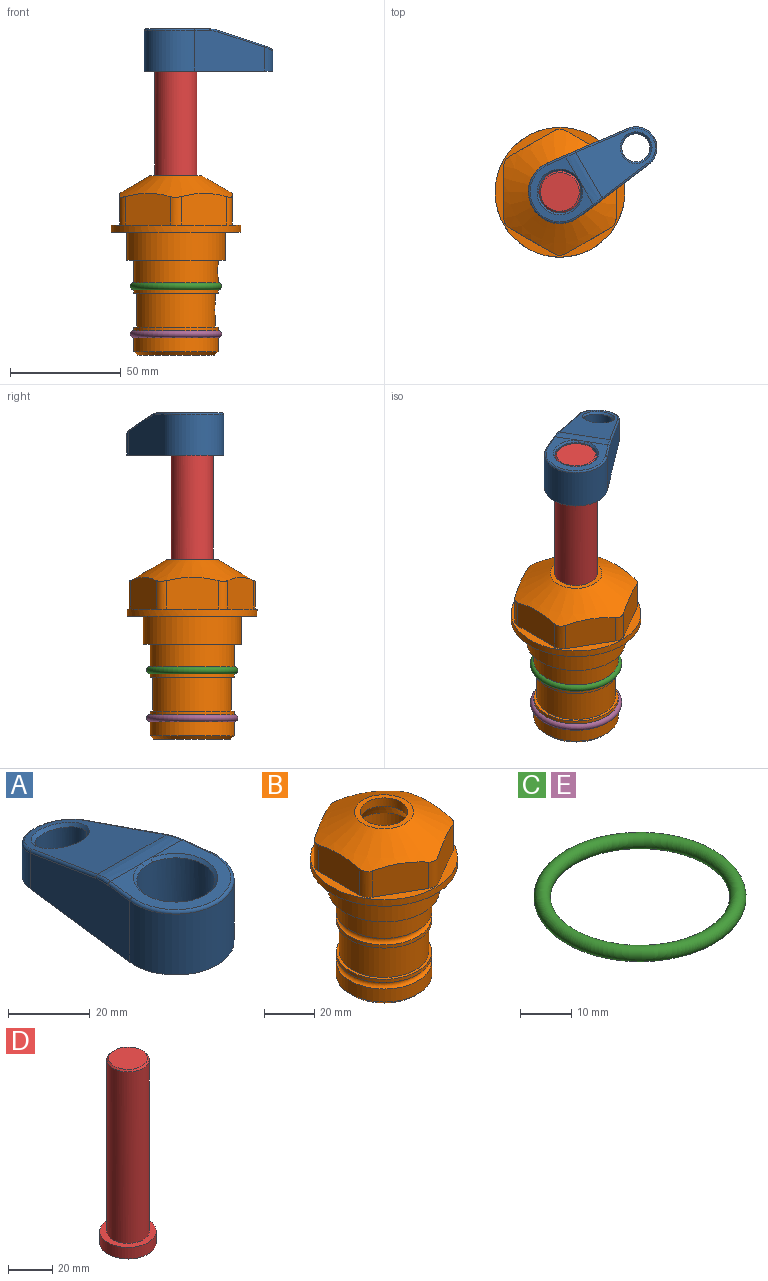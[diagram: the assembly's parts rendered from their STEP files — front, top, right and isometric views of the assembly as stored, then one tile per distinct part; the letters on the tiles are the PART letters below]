
ASSEMBLY  parts=5 mates=4
PART A: 31 faces, bbox 31.7x65.5x19.8 mm
  f0: plane 39.12x18.26mm, normal (0.99,0.12,0), area 612.2mm2, adj f1,f4,f7,f11,f13,f15
  f1: cylinder r=9.53mm len=18.91mm, axis (0,0,-1), area 296.1mm2, adj f0,f2,f7,f17
  f2: plane 39.12x18.26mm, normal (-0.99,0.12,0), area 612.2mm2, adj f1,f4,f7,f12,f14,f16
  f3: cylinder r=6.35mm len=12.7mm, axis (0,0,-1), area 362.4mm2, adj f7,f18
  f4: cylinder r=14.29mm len=28.58mm, axis (0,0,-1), area 882.2mm2, adj f0,f2,f7,f10
  f5: cylinder r=9.53mm len=19.05mm, axis (0,0,-1), area 1092.6mm2, adj f7,f19,f20
  f6: plane 26.99x23.69mm, normal (0,0,1), area 216.2mm2, adj f9,f10,f11,f12,f19
  f7: plane 63.5x28.58mm, normal (0,0,-1), area 661.8mm2, adj f0,f1,f2,f3,f4,f5,f22,f23
  f8: plane 33.52x23.6mm, normal (0,0.26,0.97), area 486mm2, adj f9,f15,f16,f17,f18
  f9: cylinder r=19.05mm len=24.72mm, axis (1,0,0), area 120.4mm2, adj f6,f8,f13,f14,f20
  f10: torus R=13.49mm, axis (0,0,1), area 59mm2, adj f4,f6,f11,f12
  f11: cylinder r=0.79mm len=8.67mm, axis (0.12,-0.99,0), area 10.8mm2, adj f0,f6,f10,f13
  f12: cylinder r=0.79mm len=8.67mm, axis (0.12,0.99,0), area 10.8mm2, adj f2,f6,f10,f14
  f13: bspline ~4.95x1.42mm, area 6.1mm2, adj f0,f9,f11,f15
  f14: bspline ~4.95x1.42mm, area 6.1mm2, adj f2,f9,f12,f16
  f15: cylinder r=0.79mm len=25.95mm, axis (0.12,-0.96,0.26), area 32.9mm2, adj f0,f8,f13,f17
  f16: cylinder r=0.79mm len=25.95mm, axis (0.12,0.96,-0.26), area 32.9mm2, adj f2,f8,f14,f17
  f17: bspline ~18.91x8.38mm, area 30mm2, adj f1,f8,f15,f16
  f18: bspline ~14.29x14.29mm, area 48.3mm2, adj f3,f8
  f19: cone r=9.53mm half-angle=45deg, axis (0,0,1), area 66.5mm2, adj f5,f6,f20
  f20: bspline ~3.22x0.96mm, area 3.5mm2, adj f5,f9,f19
  f21: plane 2.75x2.72mm, normal (0,0,-1), area 2.9mm2, adj f23,f25,f28
  f22: plane 23.05x15.88mm, normal (-0.99,-0.12,0), area 323.6mm2, adj f7,f25,f26,f27,f28,f29
  f23: plane 23.05x15.88mm, normal (0.99,-0.12,0), area 323.6mm2, adj f7,f21,f25,f27,f28,f30
  f24: cylinder r=9.53mm len=10.69mm, axis (0,0,-1), area 114.7mm2, adj f7,f27,f29,f30
  f25: cylinder r=12.7mm len=20.59mm, axis (0,0,-1), area 381.1mm2, adj f7,f21,f22,f23,f26,f28
  f26: plane 2.75x2.72mm, normal (0,0,-1), area 2.9mm2, adj f22,f25,f28
  f27: plane 19.72x18.37mm, normal (0,-0.26,-0.97), area 291.8mm2, adj f22,f23,f24,f28,f29,f30
  f28: cylinder r=15.88mm len=19.92mm, axis (1,0,0), area 54.8mm2, adj f21,f22,f23,f25,f26,f27
  f29: cylinder r=1.59mm len=11mm, axis (0,0,-1), area 34.7mm2, adj f7,f22,f24,f27
  f30: cylinder r=1.59mm len=11mm, axis (0,0,-1), area 34.7mm2, adj f7,f23,f24,f27
PART B: 36 faces, bbox 58.7x58.7x81 mm
  f0: cylinder r=17.78mm len=35.56mm, axis (0,0,1), area 1670.8mm2, adj f23,f24,f31
  f1: cylinder r=19.05mm len=38.1mm, axis (0,0,1), area 1191.9mm2, adj f26,f27,f30
  f2: plane 58.66x58.66mm, normal (0,0,-1), area 1150.6mm2, adj f3,f28
  f3: cylinder r=29.33mm len=58.66mm, axis (0,0,-1), area 585.1mm2, adj f2,f4
  f4: plane 58.66x58.66mm, normal (0,0,1), area 475.9mm2, adj f3,f5,f6,f7,f8,f9,f10,f11
  f5: plane 20.32x14.34mm, normal (-0.5,0.87,0), area 324.4mm2, adj f4,f15,f16,f17
  f6: plane 20.32x14.34mm, normal (0.5,0.87,0), area 324.4mm2, adj f4,f14,f15,f17
  f7: plane 23.48x14.34mm, normal (1,0,0), area 324.4mm2, adj f4,f13,f14,f17
  f8: plane 20.32x14.34mm, normal (0.5,-0.87,0), area 324.4mm2, adj f4,f12,f13,f17
  f9: plane 20.32x14.34mm, normal (-0.5,-0.87,0), area 324.4mm2, adj f4,f11,f12,f17
  f10: plane 23.48x14.34mm, normal (-1,0,0), area 324.4mm2, adj f4,f11,f16,f17
  f11: cylinder r=5.08mm len=12.85mm, axis (0,0,-1), area 67.2mm2, adj f4,f9,f10,f17
  f12: cylinder r=5.08mm len=12.85mm, axis (0,0,-1), area 67.2mm2, adj f4,f8,f9,f17
  f13: cylinder r=5.08mm len=12.85mm, axis (0,0,-1), area 67.2mm2, adj f4,f7,f8,f17
  f14: cylinder r=5.08mm len=12.85mm, axis (0,0,-1), area 67.2mm2, adj f4,f6,f7,f17
  f15: cylinder r=5.08mm len=12.85mm, axis (0,0,-1), area 67.2mm2, adj f4,f5,f6,f17
  f16: cylinder r=5.08mm len=12.85mm, axis (0,0,-1), area 67.2mm2, adj f4,f5,f10,f17
  f17: cone r=11.73mm half-angle=60deg, axis (0,0,-1), area 2071.8mm2, adj f5,f6,f7,f8,f9,f10,f11,f12
  f18: plane 23.46x23.46mm, normal (0,0,1), area 147.4mm2, adj f17,f35
  f19: plane 34.93x34.93mm, normal (0,0,-1), area 958mm2, adj f29
  f20: cylinder r=19.05mm len=38.1mm, axis (0,0,1), area 760.1mm2, adj f21,f29
  f21: torus R=19.05mm, axis (0,0,1), area 565.3mm2, adj f20,f22
  f22: cylinder r=19.05mm len=38.1mm, axis (0,0,1), area 190mm2, adj f21,f23
  f23: plane 38.1x38.1mm, normal (0,0,1), area 146.9mm2, adj f0,f22
  f24: plane 38.1x38.1mm, normal (0,0,-1), area 146.9mm2, adj f0,f25
  f25: cylinder r=19.05mm len=38.1mm, axis (0,0,1), area 190mm2, adj f24,f26
  f26: torus R=19.05mm, axis (0,0,1), area 565.3mm2, adj f1,f25
  f27: plane 44.45x44.45mm, normal (0,0,-1), area 411.7mm2, adj f1,f28
  f28: cylinder r=22.23mm len=44.45mm, axis (0,0,1), area 1773.5mm2, adj f2,f27
  f29: cone r=19.05mm half-angle=45deg, axis (0,0,1), area 257.5mm2, adj f19,f20
  f30: cylinder r=3.17mm len=6.75mm, axis (-1,0,0), area 128mm2, adj f1,f33
  f31: cylinder r=3.17mm len=6.35mm, axis (-1,0,0), area 102.5mm2, adj f0,f33
  f32: plane 25.4x25.4mm, normal (0,0,1), area 506.7mm2, adj f33
  f33: cylinder r=12.7mm len=66.42mm, axis (0,0,-1), area 5236.2mm2, adj f30,f31,f32,f34
  f34: cone r=9.53mm half-angle=30deg, axis (0,0,-1), area 443.4mm2, adj f33,f35
  f35: cylinder r=9.53mm len=19.05mm, axis (0,0,-1), area 240.9mm2, adj f18,f34
PART C: 1 faces, bbox 44.7x44.7x3.2 mm
  f0: torus R=19.05mm, axis (0,0,1), area 1193.9mm2
PART D: 6 faces, bbox 25.4x25.4x101.6 mm
  f0: plane 17.46x17.46mm, normal (0,0,1), area 239.5mm2, adj f5
  f1: plane 25.4x25.4mm, normal (0,0,-1), area 506.7mm2, adj f2
  f2: cylinder r=12.7mm len=25.4mm, axis (0,0,1), area 506.7mm2, adj f1,f3
  f3: plane 25.4x25.4mm, normal (0,0,1), area 221.7mm2, adj f2,f4
  f4: cylinder r=9.53mm len=94.46mm, axis (0,0,1), area 5653mm2, adj f3,f5
  f5: cone r=8.73mm half-angle=45deg, axis (0,0,-1), area 64.4mm2, adj f0,f4
PART E: same geometry as C
PLACE A rot(axis=(0,0,-1),59.8deg) t=(0,0,28.35)mm
PLACE B at identity fixed
PLACE C at identity
PLACE D rot(axis=(0,0,-1),59.8deg) t=(0,0,27.55)mm
PLACE E t=(0,0,-21.59)mm
MATE fastened D.f2 <-> A.f4  axis (0,0,1) through (0,0,91.05)mm
MATE fastened E.f0 <-> B.f0  axis (0,0,1) through (0,0,-46.1)mm
MATE fastened C.f0 <-> B.f0  axis (0,0,1) through (0,0,-24.51)mm
MATE cylindrical D.f2 <-> B.f0  axis (0,0,-1) through (0,0,-10.55)mm
